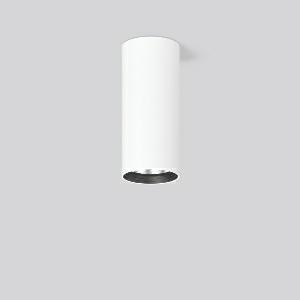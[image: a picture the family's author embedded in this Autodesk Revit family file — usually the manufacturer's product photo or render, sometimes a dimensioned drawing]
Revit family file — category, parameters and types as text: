
# Revit family: heledon_mini_a_931200_002_c6d4
name_source: partatom
category: Lighting Fixtures
units: mm (PartAtom-declared; Revit-internal decimal feet)

## family parameters
Cut with Voids When Loaded = No
Host = Face
Light Source = No
Part Type = Normal
Room Calculation Point = No
Round Connector Dimension = Use Diameter
Shared = No

## types (1)
- HELEDON mini A (1 x LED Modul 930, 2500 lm, 3000)
    Apparent Load = 20 VA
    Approval mark = CE
    CIE Flux Codes = 100 100 100 100 100
    Color Rendering = 90
    Color Temperature = 3000
    Default Elevation = 1800 mm
    Description = Series: HELEDON mini
Cylindrical surface-mounted downlight. Housing: die-cast aluminium, powder-coated. Internal ceiling frame polycarbonate with bayonet mounting. Black plastic ring and recessed LED to prevent glare from the side. Optical assembly with reflector made of MIRO-Silver with 98% total light reflection for outstanding efficiency - can be changed without tools. Best colour rendering index Ra>90. Suitable for Ceiling mounting. Easy installation with a separate ceiling frame with bayonet mounting and plug connection. Driver integrated. Connected via plug-in connector. High quality converter without flickering and stroboscopic effect. The following accessories can be mounted without use of tools: interchangeable lenses, decorative glasses, honeycomb louvre, clear and frosted diffusers, white interchangeable plastic ring. 
Colour: traffic white, matt (RAL 9016)
Diameter: 87 mm
Height: 197 mm
Lamp: LED
Socket: without socket
Colour temperature: 3000K
Colour rendering index (CRI): 92
System power: 20 W
Rated luminous flux: 2500 lm
Luminous efficiency: 125 lm/W
Control gear: Regulated power supply
Protection class: I
Type of protection: IP 20
    Height = 197 mm
    Lamp = 1 x LED Modul 930
    Lamp Light Flux = 2500 lm
    Lamp count = 1
    Length = 87 mm
    Lifetime = 50000 h
    Luminous efficacy = 125 lm/W
    Manufacturer = RZB
    ModVariant = No
    Model = 931200.002
    Mounting Place = Ceiling
    Mounting Type = Surface mounted
    Number of Poles = 1
    OnlyDefault = Yes
    Power Factor = 1
    Product Name = HELEDON mini A
    Product group = Surface mounted downlights
    ProductGroupID = 302
    Protection Class = Protection class I
    Protection Degree = IP 20
    RLX_Detail_Level = 1
    RLX_Emergency_Light_Flux = 0 lm
    RLX_Emergency_Type = 0
    RLX_Emergency_Type_DB = No
    RlxData = <blob elided: 104937 chars, md5=0559d444>
    Socket = socket
    Standby Power = 0 W
    System Light Flux = 2500 lm
    System Power = 20 W
    Type Comments = Product without accessories
    Type Image = 931188.002.jpg
    URL = http://relux.com
    VarID = ---
    Voltage = 230 V
    Voltage Range = 220-240 V
    Weight = 0.00 kg
    Width = 0 mm  [stored 0 ft]

note: [stored X ft] marks values corroborated as IEEE doubles in the binary element streams (Revit-internal decimal feet)

## geometry (parser evidence)
native form markers: Blend x4, Sweep x9
no freeform markers — native parametric forms only
